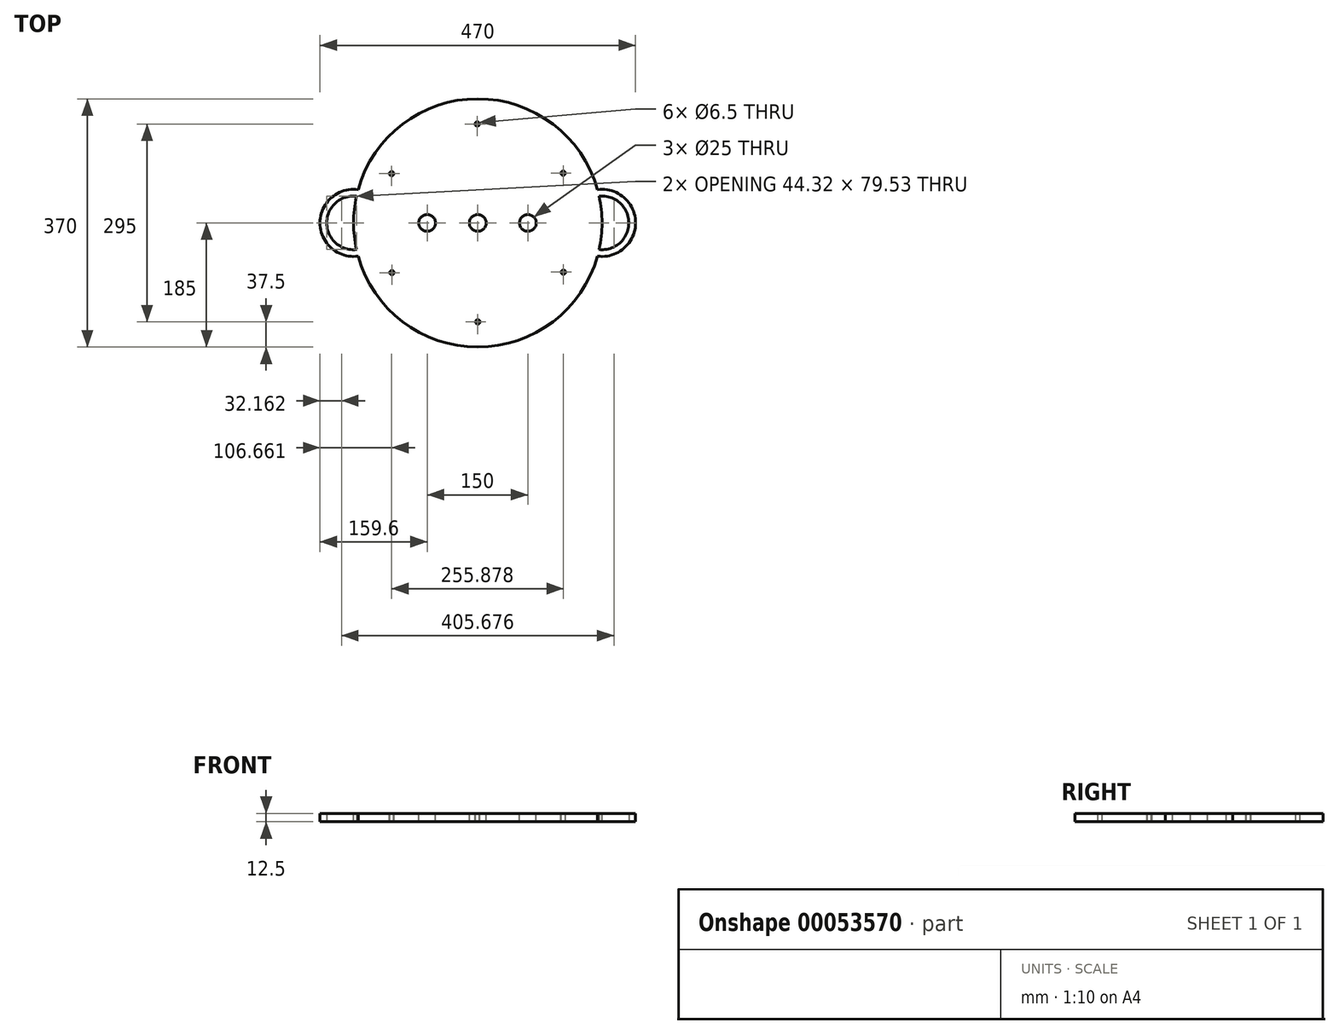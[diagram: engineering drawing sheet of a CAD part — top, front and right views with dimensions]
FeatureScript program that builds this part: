
annotation { "Feature Type Name" : "Feature", "Feature Type Description" : "" }
export const myFeature = defineFeature(function(context is Context, id is Id, definition is map)
    precondition{}
    {
        {
            var Q0;
            Q0=qCreatedBy(makeId("Top.planeOp"),FACE);
            var sketch = newSketch(context, id + "F0", { "sketchPlane" : qUnion([Q0])});
            skCircle(sketch, "E0", {"center": v(0, 0) * mm, "radius": 185 * mm});
            skCircle(sketch, "E1", {"center": v(0, -147.5) * mm, "radius": 3.25 * mm});
            skCircle(sketch, "E2.1.0", {"center": v(127.54, -73.4) * mm, "radius": 3.25 * mm});
            skCircle(sketch, "E2.2.0", {"center": v(127.14, 74.1) * mm, "radius": 3.25 * mm});
            skCircle(sketch, "E2.3.0", {"center": v(-0.8, 147.5) * mm, "radius": 3.25 * mm});
            skCircle(sketch, "E2.4.0", {"center": v(-128.34, 73.4) * mm, "radius": 3.25 * mm});
            skCircle(sketch, "E2.5.0", {"center": v(-127.94, -74.1) * mm, "radius": 3.25 * mm});
            skPoint(sketch, "E2.center", {"position": v(-0.4, 0) * mm});
            skArc(sketch, "E3", {"start": v(-178.24, 49.54) * mm, "mid": v(-235, 0) * mm, "end": v(-178.24, -49.54) * mm});
            skArc(sketch, "E4", {"start": v(-180.68, 39.77) * mm, "mid": v(-225, 0) * mm, "end": v(-180.68, -39.77) * mm});
            skArc(sketch, "E5", {"start": v(178.24, -49.54) * mm, "mid": v(235, 0) * mm, "end": v(178.24, 49.54) * mm});
            skArc(sketch, "E6", {"start": v(180.68, -39.77) * mm, "mid": v(225, 0) * mm, "end": v(180.68, 39.77) * mm});
            skCircle(sketch, "E7", {"center": v(-75.4, 0) * mm, "radius": 12.5 * mm});
            skCircle(sketch, "E8", {"center": v(0, 0) * mm, "radius": 12.5 * mm});
            skCircle(sketch, "E9", {"center": v(74.6, 0) * mm, "radius": 12.5 * mm});
            skSolve(sketch);
        }
        {
            var Q0;
            Q0=makeQuery(id+"F0.imprint","IMPRINT",FACE,{"disambiguationData":[TD([[makeQuery(id+"F0.imprint","IMPRINT",EDGE,{"derivedFrom":sQuery(id+"F0.wireOp",EDGE,"E0")}),1.0]])]});
            extrude(context, id + "F1", {"entities" : qUnion([Q0]), "endBound" : BoundingType.SYMMETRIC, "oppositeDirection" : true, "depth" : 12.5 * mm});
        }
        {
            var Q0;
            Q0 = qSketchRegion(id + "F0", true);
            extrude(context, id + "F2", {"entities" : qUnion([Q0]), "operationType" : NewBodyOperationType.ADD, "endBound" : BoundingType.SYMMETRIC, "depth" : 10 * mm});
        }
        {
            var Q0;
            Q0 = qSketchRegion(id + "F0", true);
            extrude(context, id + "F3", {"entities" : qUnion([Q0]), "operationType" : NewBodyOperationType.ADD, "endBound" : BoundingType.SYMMETRIC, "depth" : 12.5 * mm});
        }
    });
